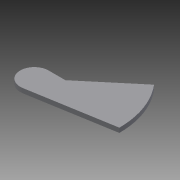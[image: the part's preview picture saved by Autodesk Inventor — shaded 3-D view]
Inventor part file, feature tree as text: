
AUTODESK INVENTOR PART (.ipt)
format: ipt  version: 2014 SP2 (Build 180246200, 246)  size: 74,752 bytes
history: native  units: mm
features: extrude x1, sketch x1
ambient origin geometry x8: Origin, YZ Plane, XZ Plane, XY Plane, X Axis, Y Axis, Z Axis, Center Point
bodies: Solid1 (feature_tree)
feature tree (2):
  extrude  "Extrusion1"  Depth=12.5mm
  sketch  "Sketch1"  dims[d1=0.0mm d4=12.5mm d7=12.5mm d8=75.0mm d9=4.0mm d10=0.0mm]
